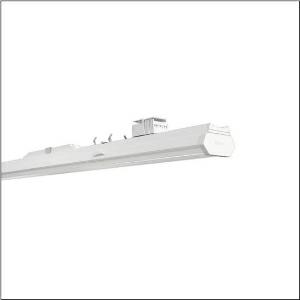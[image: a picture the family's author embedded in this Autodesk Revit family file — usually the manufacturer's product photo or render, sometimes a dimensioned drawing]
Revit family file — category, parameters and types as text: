
# Revit family: licross_r__11_protected_mo_51tp12dn59xf_cb84
name_source: partatom
category: Lighting Fixtures
units: mm (PartAtom-declared; Revit-internal decimal feet)

## family parameters
Cut with Voids When Loaded = No
Host = Face
Light Source = No
Part Type = Normal
Room Calculation Point = No
Round Connector Dimension = Use Diameter
Shared = No

## types (1)
- --- (1 x LED, 9030 lm, 56.2 W, 5000K)
    Apparent Load = 56 VA
    CIE Flux Codes = 73 92 98 99 100
    Color Rendering = 80
    Color Temperature = 5000K
    Default Elevation = 1800 mm
    Description = Licross® 11 Protected MOluminaire insert, length: 1.500mm, width: 90mm, height: 101mm, LED rated luminous flux: 9.030lm, light colour: 850, control gear: DALI 2, control gear: ECG DALI, with plug, 5-pole, with phase selection, mains connection: 220..240V, AC, 50/60Hz, halogen-free wiring, primary optical cover: cover, of PMMA, light emission: direct with ceiling illumination distribution, protection rating (complete): IP64, insulation class (complete): insulation class I (protective earthing), certification: CE, ENEC, VDE, protection symbol: D if used in an environment with conductive dust loads with corresponding accessories, permissible ambient temperature for indoor applications: -25..+40°C, reducing of maximum allowable ambient temperature of 5°C with ceiling mounting, corresponds to IFS (International Featured Standards) requirements for safety and quality in the food industry, packaging unit: 1 piece
    Height = 92 mm
    Lamp = 1 x LED
    Lamp Light Flux = 9030 lm
    Lamp Power = 56.2 W
    Lamp count = 1
    Length = 1500 mm
    Luminous efficacy = 161 lm/W
    Manufacturer = Siteco
    ModVariant = No
    Model = 51TP12DN59XF
    Mounting Place = Ceiling
    Mounting Type = Pendant
    Number of Poles = 1
    OnlyDefault = Yes
    Power Factor = 1
    Product Name = Licross® 11 Protected MO
    Product group = luminaire insert
    ProductGroupID = 902
    Protection Class = Protection class I
    Protection Degree = IP 64
    RLX_Detail_Level = 1
    RlxData = <blob elided: 23873 chars, md5=ffbe8257>
    Socket = socket
    Standby Power = 0 W
    System Light Flux = 9030 lm
    System Power = 56 W
    Type Comments = factory setting: luminous flux: 100 % | dim-lin: 254 | 370 mA
    Type Image = l_1256148.jpg
    URL = http://relux.com
    VarID = @adj_137829
    Voltage = 0 V
    Weight = 0.00 kg
    Width = 88 mm

## geometry (parser evidence)
native form markers: Blend x4, Sweep x10
no freeform markers — native parametric forms only
